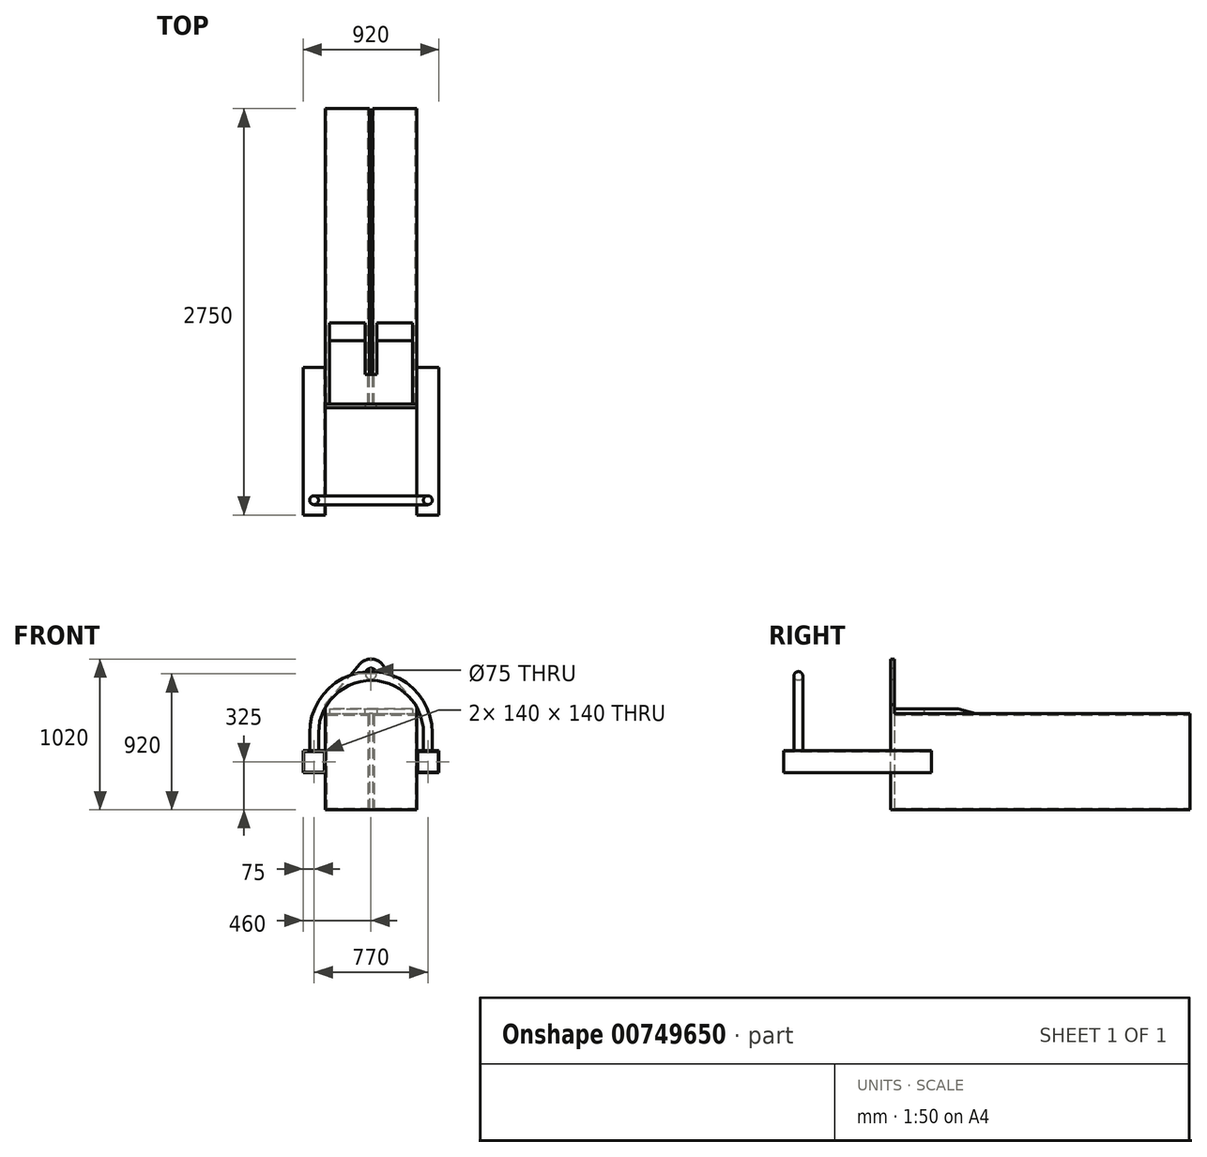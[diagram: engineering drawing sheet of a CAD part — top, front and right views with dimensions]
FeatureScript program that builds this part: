
annotation { "Feature Type Name" : "Feature", "Feature Type Description" : "" }
export const myFeature = defineFeature(function(context is Context, id is Id, definition is map)
    precondition{}
    {
        {
            var Q0;
            Q0=qCreatedBy(makeId("Front.planeOp"),FACE);
            var sketch = newSketch(context, id + "F0", { "sketchPlane" : qUnion([Q0])});
            skLineSegment(sketch, "E0.bottom", {"start": v(-310, 325) * mm, "end": v(-10, 325) * mm});
            skLineSegment(sketch, "E0.top", {"start": v(-310, -325) * mm, "end": v(-10, -325) * mm});
            skLineSegment(sketch, "E0.left", {"start": v(-310, 325) * mm, "end": v(-310, -325) * mm});
            skLineSegment(sketch, "E0.right", {"start": v(-10, 325) * mm, "end": v(-10, -325) * mm});
            skLineSegment(sketch, "E1.bottom", {"start": v(10, 325) * mm, "end": v(310, 325) * mm});
            skLineSegment(sketch, "E1.top", {"start": v(10, -325) * mm, "end": v(310, -325) * mm});
            skLineSegment(sketch, "E1.left", {"start": v(10, 325) * mm, "end": v(10, -325) * mm});
            skLineSegment(sketch, "E1.right", {"start": v(310, 325) * mm, "end": v(310, -325) * mm});
            skLineSegment(sketch, "E2.0", {"start": v(20, 315) * mm, "end": v(300, 315) * mm});
            skLineSegment(sketch, "E2.1", {"start": v(20, 315) * mm, "end": v(20, -315) * mm});
            skLineSegment(sketch, "E2.2", {"start": v(20, -315) * mm, "end": v(300, -315) * mm});
            skLineSegment(sketch, "E2.3", {"start": v(300, 315) * mm, "end": v(300, -315) * mm});
            skLineSegment(sketch, "E3.0", {"start": v(-300, 315) * mm, "end": v(-20, 315) * mm});
            skLineSegment(sketch, "E3.1", {"start": v(-300, 315) * mm, "end": v(-300, -315) * mm});
            skLineSegment(sketch, "E3.2", {"start": v(-300, -315) * mm, "end": v(-20, -315) * mm});
            skLineSegment(sketch, "E3.3", {"start": v(-20, 315) * mm, "end": v(-20, -315) * mm});
            skSolve(sketch);
        }
        {
            var Q0;
            Q0 = qSketchRegion(id + "F0", true);
            extrude(context, id + "F1", {"entities" : qUnion([Q0]), "endBound" : BoundingType.SYMMETRIC, "depth" : 2000 * mm, "offsetDistance" : 25 * mm});
        }
        {
            var Q0;
            Q0=makeQuery(id+"F1.opExtrude","SWEPT_FACE",FACE,{"disambiguationData":[OSD([sQuery(id+"F0.wireOp",EDGE,"E0.bottom")])]});
            var sketch = newSketch(context, id + "F2", { "sketchPlane" : qUnion([Q0])});
            skLineSegment(sketch, "E4", {"start": v(-280, -450) * mm, "end": v(-40, -450) * mm});
            skLineSegment(sketch, "E5", {"start": v(-40, -450) * mm, "end": v(-40, -800) * mm});
            skLineSegment(sketch, "E6", {"start": v(-40, -800) * mm, "end": v(40, -800) * mm});
            skLineSegment(sketch, "E7", {"start": v(40, -800) * mm, "end": v(40, -450) * mm});
            skLineSegment(sketch, "E8", {"start": v(40, -450) * mm, "end": v(280, -450) * mm});
            skLineSegment(sketch, "E9", {"start": v(280, -450) * mm, "end": v(280, -1000) * mm});
            skLineSegment(sketch, "E10", {"start": v(280, -1000) * mm, "end": v(-280, -1000) * mm});
            skLineSegment(sketch, "E11", {"start": v(-280, -1000) * mm, "end": v(-280, -450) * mm});
            skSolve(sketch);
        }
        {
            var Q0;
            Q0 = qSketchRegion(id + "F2", true);
            extrude(context, id + "F3", {"entities" : qUnion([Q0]), "depth" : 32 * mm, "offsetDistance" : 25 * mm});
        }
        {
            var Q0;
            Q0=makeQuery(id+"F3.opExtrude","SWEPT_FACE",FACE,{"disambiguationData":[OSD([sQuery(id+"F2.wireOp",EDGE,"E9")])]});
            var sketch = newSketch(context, id + "F4", { "sketchPlane" : qUnion([Q0])});
            skLineSegment(sketch, "E12", {"start": v(-450, 325) * mm, "end": v(-569.43, 357) * mm});
            skLineSegment(sketch, "E13", {"start": v(-569.43, 357) * mm, "end": v(-450, 357) * mm});
            skLineSegment(sketch, "E14", {"start": v(-450, 357) * mm, "end": v(-450, 325) * mm});
            skSolve(sketch);
        }
        {
            var Q0;
            Q0 = qSketchRegion(id + "F4", true);
            var Q1;
            Q1=makeQuery(id+"F3.opExtrude","SWEPT_FACE",FACE,{"disambiguationData":[OSD([sQuery(id+"F2.wireOp",EDGE,"E11")])]});
            extrude(context, id + "F5", {"entities" : qUnion([Q0]), "operationType" : NewBodyOperationType.REMOVE, "endBound" : BoundingType.UP_TO_SURFACE, "oppositeDirection" : true, "depth" : 25 * mm, "endBoundEntityFace" : qUnion([Q1]), "offsetDistance" : 25 * mm});
        }
        {
            var Q0;
            Q0=makeQuery(id+"F3.opExtrude","SWEPT_FACE",FACE,{"disambiguationData":[OSD([sQuery(id+"F2.wireOp",EDGE,"E10")])]});
            var sketch = newSketch(context, id + "F6", { "sketchPlane" : qUnion([Q0])});
            skLineSegment(sketch, "E15.bottom", {"start": v(310, -325) * mm, "end": v(-310, -325) * mm});
            skLineSegment(sketch, "E15.top", {"start": v(310, 385) * mm, "end": v(-310, 385) * mm, "construction": true});
            skLineSegment(sketch, "E15.left", {"start": v(310, -325) * mm, "end": v(310, 385) * mm});
            skLineSegment(sketch, "E15.right", {"start": v(-310, -325) * mm, "end": v(-310, 385) * mm});
            skCircle(sketch, "E16", {"center": v(0, 595) * mm, "radius": 37.5 * mm});
            skArc(sketch, "E17", {"start": v(76.16, 659.8) * mm, "mid": v(0, 695) * mm, "end": v(-76.16, 659.8) * mm});
            skLineSegment(sketch, "E18", {"start": v(-310, 385) * mm, "end": v(-76.16, 659.8) * mm});
            skLineSegment(sketch, "E19", {"start": v(310, 385) * mm, "end": v(76.16, 659.8) * mm});
            skSolve(sketch);
        }
        {
            var Q0;
            Q0 = qSketchRegion(id + "F6", true);
            extrude(context, id + "F7", {"entities" : qUnion([Q0]), "depth" : 25 * mm, "offsetDistance" : 25 * mm});
        }
        {
            var Q0;
            Q0=makeQuery(id+"F1.opExtrude","SWEPT_BODY",BODY,{"disambiguationData":[OSD([sQuery(id+"F0.wireOp",EDGE,"E0.bottom"),sQuery(id+"F0.wireOp",EDGE,"E0.top"),sQuery(id+"F0.wireOp",EDGE,"E0.left"),sQuery(id+"F0.wireOp",EDGE,"E0.right"),sQuery(id+"F0.wireOp",EDGE,"E3.0"),sQuery(id+"F0.wireOp",EDGE,"E3.1"),sQuery(id+"F0.wireOp",EDGE,"E3.2"),sQuery(id+"F0.wireOp",EDGE,"E3.3")])]});
            var Q1;
            Q1=makeQuery(id+"F1.opExtrude","SWEPT_BODY",BODY,{"disambiguationData":[OSD([sQuery(id+"F0.wireOp",EDGE,"E1.bottom"),sQuery(id+"F0.wireOp",EDGE,"E1.top"),sQuery(id+"F0.wireOp",EDGE,"E1.left"),sQuery(id+"F0.wireOp",EDGE,"E1.right"),sQuery(id+"F0.wireOp",EDGE,"E2.0"),sQuery(id+"F0.wireOp",EDGE,"E2.1"),sQuery(id+"F0.wireOp",EDGE,"E2.2"),sQuery(id+"F0.wireOp",EDGE,"E2.3")])]});
            var Q2;
            Q2=makeQuery(id+"F3.opExtrude","SWEPT_BODY",BODY,{"disambiguationData":[OSD([sQuery(id+"F2.wireOp",EDGE,"E4"),sQuery(id+"F2.wireOp",EDGE,"E5"),sQuery(id+"F2.wireOp",EDGE,"E6"),sQuery(id+"F2.wireOp",EDGE,"E7"),sQuery(id+"F2.wireOp",EDGE,"E8"),sQuery(id+"F2.wireOp",EDGE,"E9"),sQuery(id+"F2.wireOp",EDGE,"E10"),sQuery(id+"F2.wireOp",EDGE,"E11")])]});
            var Q3;
            Q3=makeQuery(id+"F7.opExtrude","SWEPT_BODY",BODY,{"disambiguationData":[OSD([sQuery(id+"F6.wireOp",EDGE,"E15.bottom"),sQuery(id+"F6.wireOp",EDGE,"E15.left"),sQuery(id+"F6.wireOp",EDGE,"E15.right"),sQuery(id+"F6.wireOp",EDGE,"E16"),sQuery(id+"F6.wireOp",EDGE,"E17"),sQuery(id+"F6.wireOp",EDGE,"E18"),sQuery(id+"F6.wireOp",EDGE,"E19")])]});
            booleanBodies(context, id + "F8", {"operationType" : BooleanOperationType.UNION, "tools" : qUnion([Q0, Q1, Q2, Q3])});
        }
        {
            var Q0;
            Q0=qCreatedBy(makeId("Front.planeOp"),FACE);
            cPlane(context, id + "F9", {"entities" : qUnion([Q0]), "cplaneType" : CPlaneType.OFFSET, "offset" : 750 * mm, "width" : 150 * mm, "height" : 150 * mm});
        }
        {
            var Q0;
            Q0=qCreatedBy(id+"F9.planeOp",FACE);
            var sketch = newSketch(context, id + "F10", { "sketchPlane" : qUnion([Q0])});
            skLineSegment(sketch, "E20.bottom", {"start": v(310, 75) * mm, "end": v(460, 75) * mm});
            skLineSegment(sketch, "E20.top", {"start": v(310, -75) * mm, "end": v(460, -75) * mm});
            skLineSegment(sketch, "E20.left", {"start": v(310, 75) * mm, "end": v(310, -75) * mm});
            skLineSegment(sketch, "E20.right", {"start": v(460, 75) * mm, "end": v(460, -75) * mm});
            skLineSegment(sketch, "E21.bottom", {"start": v(-460, 75) * mm, "end": v(-310, 75) * mm});
            skLineSegment(sketch, "E21.top", {"start": v(-460, -75) * mm, "end": v(-310, -75) * mm});
            skLineSegment(sketch, "E21.left", {"start": v(-460, 75) * mm, "end": v(-460, -75) * mm});
            skLineSegment(sketch, "E21.right", {"start": v(-310, 75) * mm, "end": v(-310, -75) * mm});
            skLineSegment(sketch, "E22.0", {"start": v(-455, 70) * mm, "end": v(-315, 70) * mm});
            skLineSegment(sketch, "E22.1", {"start": v(-455, 70) * mm, "end": v(-455, -70) * mm});
            skLineSegment(sketch, "E22.2", {"start": v(-455, -70) * mm, "end": v(-315, -70) * mm});
            skLineSegment(sketch, "E22.3", {"start": v(-315, 70) * mm, "end": v(-315, -70) * mm});
            skLineSegment(sketch, "E23.0", {"start": v(315, 70) * mm, "end": v(455, 70) * mm});
            skLineSegment(sketch, "E23.1", {"start": v(315, 70) * mm, "end": v(315, -70) * mm});
            skLineSegment(sketch, "E23.2", {"start": v(315, -70) * mm, "end": v(455, -70) * mm});
            skLineSegment(sketch, "E23.3", {"start": v(455, 70) * mm, "end": v(455, -70) * mm});
            skSolve(sketch);
        }
        {
            var Q0;
            Q0 = qSketchRegion(id + "F10", true);
            extrude(context, id + "F11", {"entities" : qUnion([Q0]), "operationType" : NewBodyOperationType.ADD, "depth" : 1000 * mm, "offsetDistance" : 25 * mm});
        }
        {
            var Q0;
            Q0=makeQuery(id+"F11.opExtrude","SWEPT_FACE",FACE,{"disambiguationData":[OSD([sQuery(id+"F10.wireOp",EDGE,"E20.bottom")])]});
            var sketch = newSketch(context, id + "F12", { "sketchPlane" : qUnion([Q0])});
            skLineSegment(sketch, "E24", {"start": v(385, -1750) * mm, "end": v(385, -750) * mm, "construction": true});
            skCircle(sketch, "E25", {"center": v(385, -1650) * mm, "radius": 30 * mm});
            skSolve(sketch);
        }
        {
            var Q0;
            Q0=makeQuery(id+"F11.opExtrude","CAP_FACE",FACE,{"disambiguationData":[OSD([sQuery(id+"F10.wireOp",EDGE,"E20.bottom"),sQuery(id+"F10.wireOp",EDGE,"E20.top"),sQuery(id+"F10.wireOp",EDGE,"E20.left"),sQuery(id+"F10.wireOp",EDGE,"E20.right"),sQuery(id+"F10.wireOp",EDGE,"E23.0"),sQuery(id+"F10.wireOp",EDGE,"E23.1"),sQuery(id+"F10.wireOp",EDGE,"E23.2"),sQuery(id+"F10.wireOp",EDGE,"E23.3")])],"isStart":false});
            cPlane(context, id + "F13", {"entities" : qUnion([Q0]), "cplaneType" : CPlaneType.OFFSET, "offset" : 100 * mm, "oppositeDirection" : true, "width" : 150 * mm, "height" : 150 * mm});
        }
        {
            var Q0;
            Q0=qCreatedBy(id+"F13.planeOp",FACE);
            var sketch = newSketch(context, id + "F14", { "sketchPlane" : qUnion([Q0])});
            skLineSegment(sketch, "E26", {"start": v(385, 75) * mm, "end": v(385, 195) * mm});
            skLineSegment(sketch, "E27", {"start": v(-385, 75) * mm, "end": v(-385, 195) * mm});
            skLineSegment(sketch, "E28", {"start": v(-385, 195) * mm, "end": v(385, 195) * mm, "construction": true});
            skArc(sketch, "E29", {"start": v(385, 195) * mm, "mid": v(0, 580) * mm, "end": v(-385, 195) * mm});
            skSolve(sketch);
        }
        {
            var Q0;
            Q0=makeQuery(id+"F12.imprint","IMPRINT",FACE,{"disambiguationData":[TD([[makeQuery(id+"F12.imprint","IMPRINT",EDGE,{"derivedFrom":sQuery(id+"F12.wireOp",EDGE,"E25")}),1.0]])]});
            var Q1;
            Q1=sQuery(id+"F14.wireOp",EDGE,"E26");
            var Q2;
            Q2=sQuery(id+"F14.wireOp",EDGE,"E29");
            var Q3;
            Q3=sQuery(id+"F14.wireOp",EDGE,"E27");
            sweep(context, id + "F15", {"operationType" : NewBodyOperationType.ADD, "profiles" : qUnion([Q0]), "path" : qUnion([Q1, Q2, Q3])});
        }
    });
